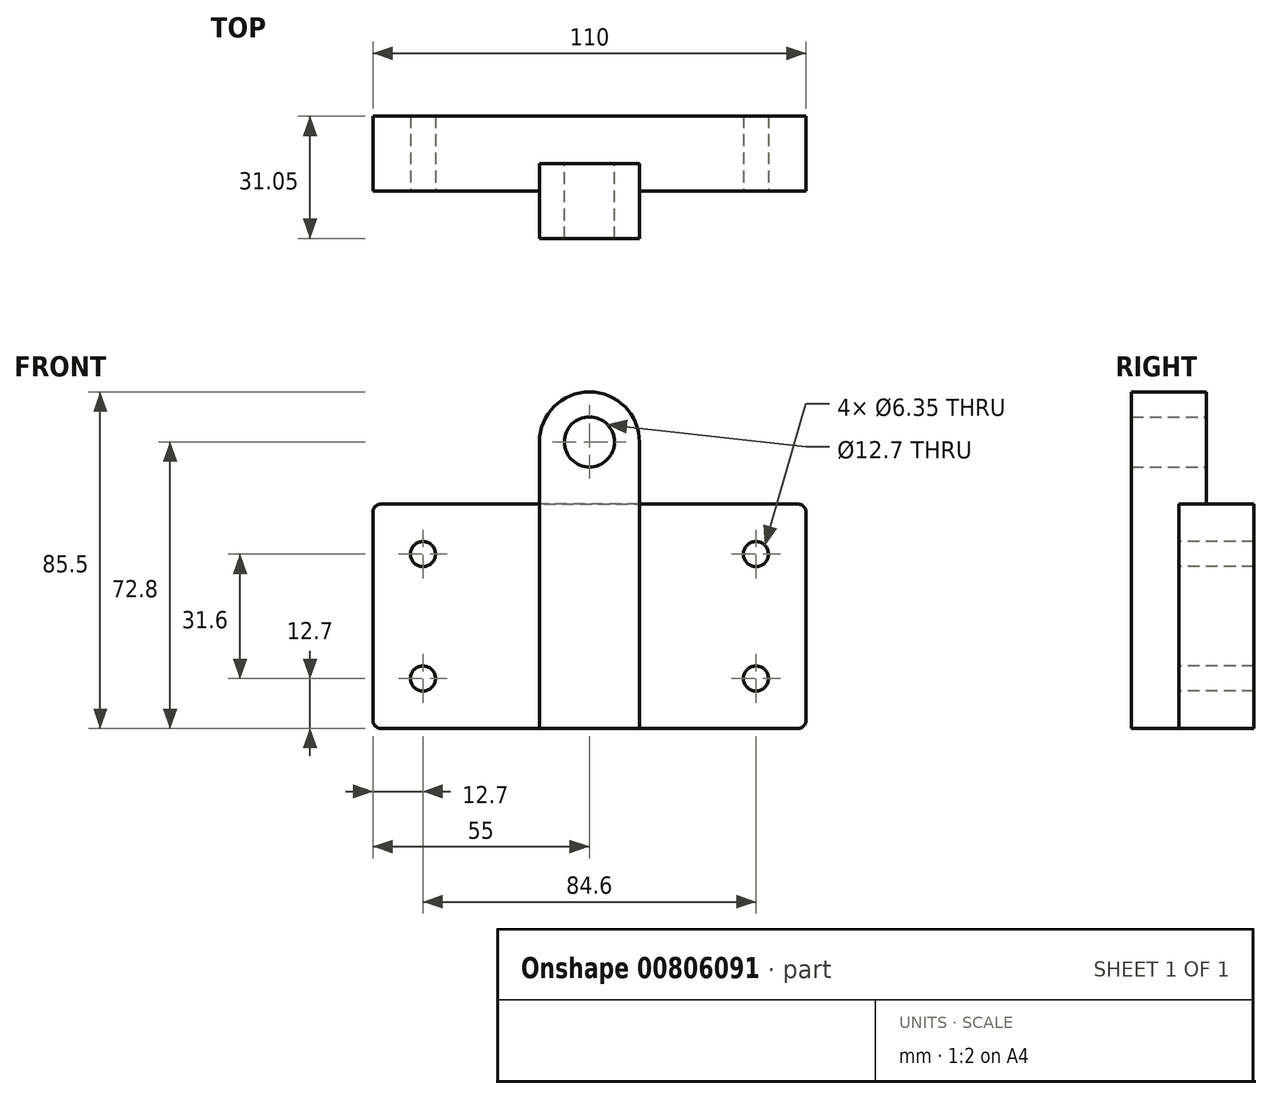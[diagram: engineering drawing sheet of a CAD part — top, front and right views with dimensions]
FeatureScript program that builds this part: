
annotation { "Feature Type Name" : "Feature", "Feature Type Description" : "" }
export const myFeature = defineFeature(function(context is Context, id is Id, definition is map)
    precondition{}
    {
        {
            var Q0;
            Q0=qCreatedBy(makeId("Front.planeOp"),FACE);
            var sketch = newSketch(context, id + "F0", { "sketchPlane" : qUnion([Q0])});
            skLineSegment(sketch, "E0.bottom", {"start": v(-53, 28.5) * mm, "end": v(53, 28.5) * mm});
            skLineSegment(sketch, "E0.top", {"start": v(-53, -28.5) * mm, "end": v(53, -28.5) * mm});
            skLineSegment(sketch, "E0.left", {"start": v(-55, 26.5) * mm, "end": v(-55, -26.5) * mm});
            skLineSegment(sketch, "E0.right", {"start": v(55, 26.5) * mm, "end": v(55, -26.5) * mm});
            skPoint(sketch, "E0.middle", {"position": v(0, 0) * mm});
            skPoint(sketch, "E1.visualSharp", {"position": v(-55, 28.5) * mm});
            skArc(sketch, "E1.filletArc", {"start": v(-53, 28.5) * mm, "mid": v(-54.41, 27.91) * mm, "end": v(-55, 26.5) * mm});
            skPoint(sketch, "E2.visualSharp", {"position": v(-55, -28.5) * mm});
            skArc(sketch, "E2.filletArc", {"start": v(-55, -26.5) * mm, "mid": v(-54.41, -27.91) * mm, "end": v(-53, -28.5) * mm});
            skPoint(sketch, "E3.visualSharp", {"position": v(55, 28.5) * mm});
            skArc(sketch, "E3.filletArc", {"start": v(55, 26.5) * mm, "mid": v(54.41, 27.91) * mm, "end": v(53, 28.5) * mm});
            skPoint(sketch, "E4.visualSharp", {"position": v(55, -28.5) * mm});
            skArc(sketch, "E4.filletArc", {"start": v(53, -28.5) * mm, "mid": v(54.41, -27.91) * mm, "end": v(55, -26.5) * mm});
            skLineSegment(sketch, "E5.bottom", {"start": v(-12.7, 57) * mm, "end": v(12.7, 57) * mm});
            skLineSegment(sketch, "E5.top", {"start": v(-12.7, -28.5) * mm, "end": v(12.7, -28.5) * mm});
            skLineSegment(sketch, "E5.left", {"start": v(-12.7, 57) * mm, "end": v(-12.7, -28.5) * mm});
            skLineSegment(sketch, "E5.right", {"start": v(12.7, 57) * mm, "end": v(12.7, -28.5) * mm});
            skLineSegment(sketch, "E6", {"start": v(0, 0) * mm, "end": v(0, -28.5) * mm, "construction": true});
            skCircle(sketch, "E7", {"center": v(0, 44.3) * mm, "radius": 12.7 * mm});
            skCircle(sketch, "E8", {"center": v(0, 44.3) * mm, "radius": 6.35 * mm});
            skCircle(sketch, "E9", {"center": v(-42.3, 15.8) * mm, "radius": 3.18 * mm});
            skCircle(sketch, "E10", {"center": v(-42.3, -15.8) * mm, "radius": 3.18 * mm});
            skCircle(sketch, "E11.MirrorC", {"center": v(42.3, -15.8) * mm, "radius": 3.18 * mm});
            skCircle(sketch, "E12.MirrorC", {"center": v(42.3, 15.8) * mm, "radius": 3.18 * mm});
            skSolve(sketch);
        }
        {
            var Q0;
            {var subQ0=sQuery(id+"F0.wireOp",EDGE,"E5.right");var subQ1=sQuery(id+"F0.wireOp",EDGE,"E0.bottom");var subQ2=makeQuery(id+"F0.imprint","INTERSECT",VERTEX,{"derivedFrom":[subQ1,subQ0]});Q0=makeQuery(id+"F0.imprint","IMPRINT",FACE,{"disambiguationData":[TD([[makeQuery(id+"F0.imprint","IMPRINT",EDGE,{"disambiguationData":[TD([[subQ2,1.0]])],"derivedFrom":subQ1}),-1.0]])]});}
            var Q1;
            Q1=makeQuery(id+"F0.imprint","IMPRINT",FACE,{"disambiguationData":[TD([[makeQuery(id+"F0.imprint","IMPRINT",EDGE,{"derivedFrom":sQuery(id+"F0.wireOp",EDGE,"E0.left")}),1.0]])]});
            var Q2;
            Q2=makeQuery(id+"F0.imprint","IMPRINT",FACE,{"disambiguationData":[TD([[makeQuery(id+"F0.imprint","IMPRINT",EDGE,{"derivedFrom":sQuery(id+"F0.wireOp",EDGE,"E0.right")}),-1.0]])]});
            extrude(context, id + "F1", {"entities" : qUnion([Q0, Q1, Q2]), "oppositeDirection" : true, "depth" : 12 * mm, "offsetDistance" : 25.4 * mm, "hasSecondDirection" : true, "secondDirectionOppositeDirection" : false, "secondDirectionDepth" : 19.05 * mm - 12 * mm});
        }
        {
            var Q0;
            {var subQ0=sQuery(id+"F0.wireOp",EDGE,"E5.right");var subQ1=sQuery(id+"F0.wireOp",EDGE,"E0.bottom");var subQ2=makeQuery(id+"F0.imprint","INTERSECT",VERTEX,{"derivedFrom":[subQ1,subQ0]});Q0=makeQuery(id+"F0.imprint","IMPRINT",FACE,{"disambiguationData":[TD([[makeQuery(id+"F0.imprint","IMPRINT",EDGE,{"disambiguationData":[TD([[subQ2,1.0]])],"derivedFrom":subQ1}),-1.0]])]});}
            var Q1;
            {var subQ0=sQuery(id+"F0.wireOp",EDGE,"E5.right");var subQ1=sQuery(id+"F0.wireOp",EDGE,"E0.bottom");var subQ2=makeQuery(id+"F0.imprint","INTERSECT",VERTEX,{"derivedFrom":[subQ1,subQ0]});Q1=makeQuery(id+"F0.imprint","IMPRINT",FACE,{"disambiguationData":[TD([[makeQuery(id+"F0.imprint","IMPRINT",EDGE,{"disambiguationData":[TD([[subQ2,1.0]])],"derivedFrom":subQ1}),1.0]])]});}
            var Q2;
            Q2=makeQuery(id+"F0.imprint","IMPRINT",FACE,{"disambiguationData":[TD([[makeQuery(id+"F0.imprint","IMPRINT",EDGE,{"derivedFrom":sQuery(id+"F0.wireOp",EDGE,"E8")}),-1.0]])]});
            extrude(context, id + "F2", {"entities" : qUnion([Q0, Q1, Q2]), "operationType" : NewBodyOperationType.ADD, "depth" : 19.05 * mm, "offsetDistance" : 25.4 * mm});
        }
    });
